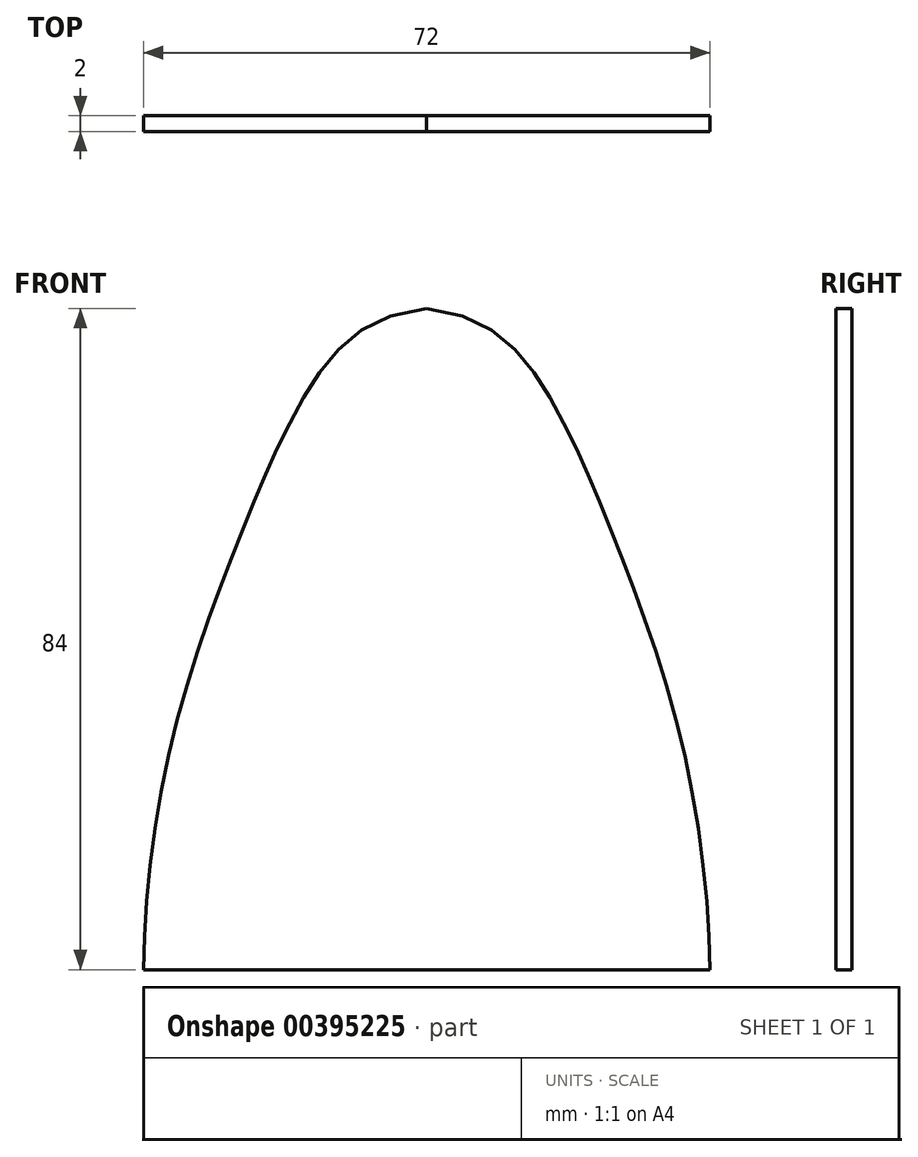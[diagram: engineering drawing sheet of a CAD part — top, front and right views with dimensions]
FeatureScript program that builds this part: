
annotation { "Feature Type Name" : "Feature", "Feature Type Description" : "" }
export const myFeature = defineFeature(function(context is Context, id is Id, definition is map)
    precondition{}
    {
        {
            var Q0;
            Q0=qCreatedBy(makeId("Front.planeOp"),FACE);
            var sketch = newSketch(context, id + "F0", { "sketchPlane" : qUnion([Q0])});
            skLineSegment(sketch, "E0", {"start": v(0, 0) * mm, "end": v(36, 0) * mm});
            skLineSegment(sketch, "E1", {"start": v(0, 0) * mm, "end": v(0, 84) * mm, "construction": true});
            skFitSpline(sketch, "E2", {"points": [v(0, 84) * mm, v(16.27, 71.57) * mm, v(24.09, 54.1) * mm, v(32.37, 29.03) * mm, v(36, 0) * mm], "startDerivative": vector(116.54, -10.26) * mm, "endDerivative": vector(1.3, -95.5) * mm});
            skFitSpline(sketch, "E3.MirrorCS", {"points": [v(0, 84) * mm, v(-16.27, 71.57) * mm, v(-24.09, 54.1) * mm, v(-32.37, 29.03) * mm, v(-36, 0) * mm], "startDerivative": vector(-116.54, -10.26) * mm, "endDerivative": vector(-1.3, -95.5) * mm});
            skLineSegment(sketch, "E4.MirrorCS", {"start": v(0, 0) * mm, "end": v(-36, 0) * mm});
            skLineSegment(sketch, "E5", {"start": v(-32.37, 29.03) * mm, "end": v(32.37, 29.03) * mm, "construction": true});
            skLineSegment(sketch, "E6", {"start": v(-24.09, 54.1) * mm, "end": v(24.09, 54.1) * mm, "construction": true});
            skLineSegment(sketch, "E7", {"start": v(-16.27, 71.57) * mm, "end": v(16.27, 71.57) * mm, "construction": true});
            skLineSegment(sketch, "E8", {"start": v(24.09, 54.1) * mm, "end": v(24.09, 0) * mm, "construction": true});
            skLineSegment(sketch, "E9", {"start": v(32.37, 29.03) * mm, "end": v(32.37, 0) * mm, "construction": true});
            skLineSegment(sketch, "E10", {"start": v(16.27, 71.57) * mm, "end": v(16.27, 0) * mm, "construction": true});
            skSolve(sketch);
        }
        {
            var Q0;
            Q0=makeQuery(id+"F0.imprint","IMPRINT",FACE,{"disambiguationData":[TD([[makeQuery(id+"F0.imprint","IMPRINT",EDGE,{"derivedFrom":sQuery(id+"F0.wireOp",EDGE,"E0")}),1.0]])]});
            extrude(context, id + "F1", {"entities" : qUnion([Q0]), "depth" : 2 * mm});
        }
    });
